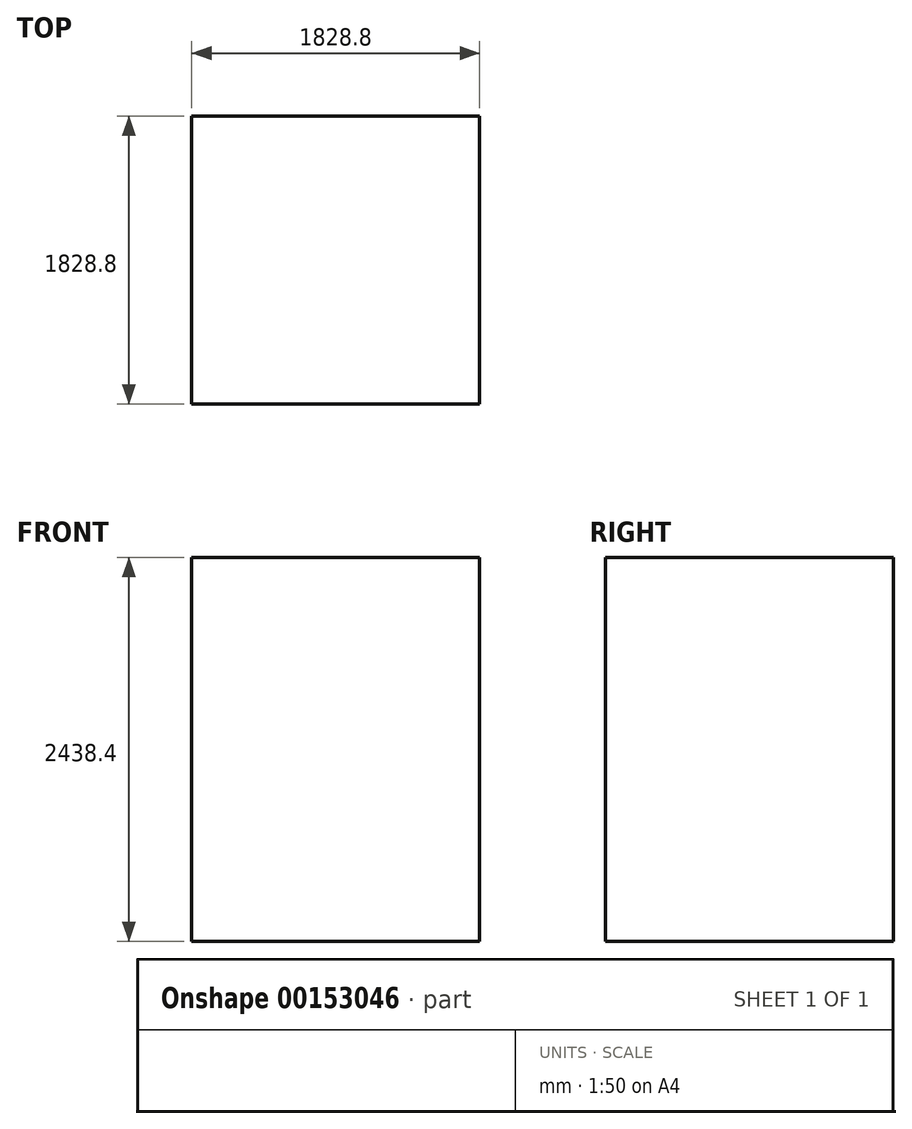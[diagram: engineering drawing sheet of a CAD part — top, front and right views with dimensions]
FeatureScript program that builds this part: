
annotation { "Feature Type Name" : "Feature", "Feature Type Description" : "" }
export const myFeature = defineFeature(function(context is Context, id is Id, definition is map)
    precondition{}
    {
        {
            var Q0;
            Q0=qCreatedBy(makeId("Top.planeOp"),FACE);
            var sketch = newSketch(context, id + "F0", { "sketchPlane" : qUnion([Q0])});
            skLineSegment(sketch, "E0.bottom", {"start": v(0, 305.22) * mm, "end": v(-1828.8, 305.22) * mm});
            skLineSegment(sketch, "E0.top", {"start": v(0, -1523.58) * mm, "end": v(-1828.8, -1523.58) * mm});
            skLineSegment(sketch, "E0.left", {"start": v(0, 305.22) * mm, "end": v(0, -1523.58) * mm});
            skLineSegment(sketch, "E0.right", {"start": v(-1828.8, 305.22) * mm, "end": v(-1828.8, -1523.58) * mm});
            skSolve(sketch);
        }
        {
            var Q0;
            Q0 = qSketchRegion(id + "F0", true);
            extrude(context, id + "F1", {"entities" : qUnion([Q0]), "depth" : 2438.4 * mm});
        }
    });
